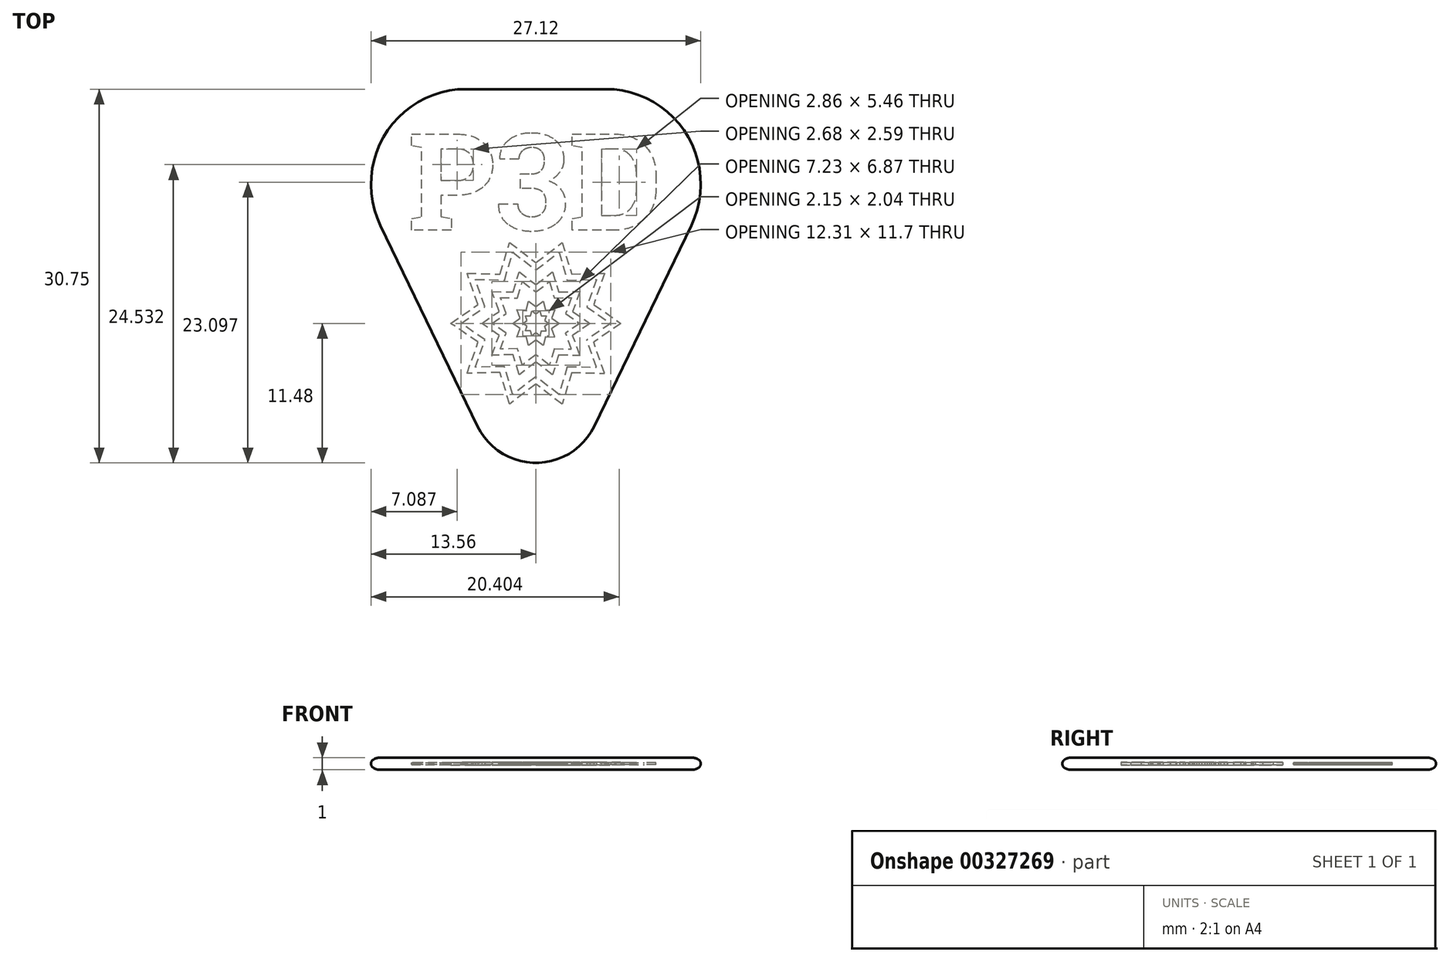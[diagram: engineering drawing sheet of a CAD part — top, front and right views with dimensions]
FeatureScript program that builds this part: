
annotation { "Feature Type Name" : "Feature", "Feature Type Description" : "" }
export const myFeature = defineFeature(function(context is Context, id is Id, definition is map)
    precondition{}
    {
        {
            var Q0;
            Q0=qCreatedBy(makeId("Top.planeOp"),FACE);
            var sketch = newSketch(context, id + "F0", { "sketchPlane" : qUnion([Q0])});
            skLineSegment(sketch, "E0", {"start": v(-5.74, 12.45) * mm, "end": v(5.74, 12.45) * mm});
            skLineSegment(sketch, "E1", {"start": v(12.95, 0.97) * mm, "end": v(4.95, -15.56) * mm});
            skLineSegment(sketch, "E2", {"start": v(-4.95, -15.56) * mm, "end": v(-12.95, 0.97) * mm});
            skPoint(sketch, "E3.visualSharp", {"position": v(-18.5, 12.45) * mm});
            skArc(sketch, "E3.filletArc", {"start": v(-5.74, 12.45) * mm, "mid": v(-12.52, 8.7) * mm, "end": v(-12.95, 0.97) * mm});
            skPoint(sketch, "E4.visualSharp", {"position": v(18.5, 12.45) * mm});
            skArc(sketch, "E4.filletArc", {"start": v(12.95, 0.97) * mm, "mid": v(12.52, 8.7) * mm, "end": v(5.74, 12.45) * mm});
            skPoint(sketch, "E5.visualSharp", {"position": v(0, -25.8) * mm});
            skArc(sketch, "E5.filletArc", {"start": v(-4.95, -15.56) * mm, "mid": v(0, -18.66) * mm, "end": v(4.95, -15.56) * mm});
            skSolve(sketch);
        }
        {
            var Q0;
            Q0=makeQuery(id+"F0.imprint","IMPRINT",FACE,{"disambiguationData":[TD([[makeQuery(id+"F0.imprint","IMPRINT",EDGE,{"derivedFrom":sQuery(id+"F0.wireOp",EDGE,"E0")}),-1.0]])]});
            extrude(context, id + "F1", {"entities" : qUnion([Q0]), "endBound" : BoundingType.SYMMETRIC, "depth" : 1 * mm, "offsetDistance" : 25 * mm});
        }
        {
            var Q0;
            Q0=makeQuery(id+"F1.opExtrude","CAP_EDGE",EDGE,{"disambiguationData":[OSD([sQuery(id+"F0.wireOp",EDGE,"E1")])],"isStart":false});
            var Q1;
            Q1=makeQuery(id+"F1.opExtrude","CAP_EDGE",EDGE,{"disambiguationData":[OSD([sQuery(id+"F0.wireOp",EDGE,"E1")])],"isStart":true});
            chamfer(context, id + "F2", {"entities" : qUnion([Q0, Q1]), "chamferType" : ChamferType.OFFSET_ANGLE, "width" : 0.5 * mm, "oppositeDirection" : false, "angle" : 45 * degree, "tangentPropagation" : true});
        }
        {
            var Q0;
            {var subQ0=sQuery(id+"F0.wireOp",EDGE,"E2");Q0=makeQuery(id+"F2.opChamfer","BLEND_EDGE",EDGE,{"blendedFrom":[makeQuery(id+"F1.opExtrude","CAP_EDGE",EDGE,{"disambiguationData":[OSD([subQ0])],"isStart":false}),makeQuery(id+"F1.opExtrude","CAP_FACE",FACE,{"disambiguationData":[OSD([sQuery(id+"F0.wireOp",EDGE,"E0"),sQuery(id+"F0.wireOp",EDGE,"E1"),subQ0,sQuery(id+"F0.wireOp",EDGE,"E3.filletArc"),sQuery(id+"F0.wireOp",EDGE,"E4.filletArc"),sQuery(id+"F0.wireOp",EDGE,"E5.filletArc")])],"isStart":false})],"blendedInto":[makeQuery(id+"F1.opExtrude","CAP_FACE",FACE,{"disambiguationData":[OSD([sQuery(id+"F0.wireOp",EDGE,"E0"),sQuery(id+"F0.wireOp",EDGE,"E1"),subQ0,sQuery(id+"F0.wireOp",EDGE,"E3.filletArc"),sQuery(id+"F0.wireOp",EDGE,"E4.filletArc"),sQuery(id+"F0.wireOp",EDGE,"E5.filletArc")])],"isStart":false})]});}
            var Q1;
            {var subQ0=sQuery(id+"F0.wireOp",EDGE,"E1");Q1=makeQuery(id+"F2.opChamfer","BLEND_EDGE",EDGE,{"blendedFrom":[makeQuery(id+"F1.opExtrude","CAP_EDGE",EDGE,{"disambiguationData":[OSD([subQ0])],"isStart":true}),makeQuery(id+"F1.opExtrude","CAP_FACE",FACE,{"disambiguationData":[OSD([sQuery(id+"F0.wireOp",EDGE,"E0"),subQ0,sQuery(id+"F0.wireOp",EDGE,"E2"),sQuery(id+"F0.wireOp",EDGE,"E3.filletArc"),sQuery(id+"F0.wireOp",EDGE,"E4.filletArc"),sQuery(id+"F0.wireOp",EDGE,"E5.filletArc")])],"isStart":true})],"blendedInto":[makeQuery(id+"F1.opExtrude","CAP_FACE",FACE,{"disambiguationData":[OSD([sQuery(id+"F0.wireOp",EDGE,"E0"),subQ0,sQuery(id+"F0.wireOp",EDGE,"E2"),sQuery(id+"F0.wireOp",EDGE,"E3.filletArc"),sQuery(id+"F0.wireOp",EDGE,"E4.filletArc"),sQuery(id+"F0.wireOp",EDGE,"E5.filletArc")])],"isStart":true})]});}
            fillet(context, id + "F3", {"entities" : qUnion([Q0, Q1]), "radius" : 1 * mm, "tangentPropagation" : true, "allowEdgeOverflow" : false});
        }
        {
            var Q0;
            Q0=qCreatedBy(makeId("Top.planeOp"),FACE);
            var sketch = newSketch(context, id + "F4", { "sketchPlane" : qUnion([Q0])});
            skText(sketch, "E6", { "text": "P3D", "fontName": "RobotoSlab-Bold.ttf"});
            const initialGuessF4  = {"E6": [-0.01054, 0.00067, 1, 0, 0.008]};
            skSetInitialGuess(sketch, initialGuessF4);
            skSolve(sketch);
        }
        {
            var Q0;
            Q0=qSketchRegion(id+"F4",true);
            extrude(context, id + "F5", {"entities" : qUnion([Q0]), "operationType" : NewBodyOperationType.REMOVE, "endBound" : BoundingType.SYMMETRIC, "oppositeDirection" : true, "depth" : 0.18 * mm, "offsetDistance" : 25 * mm});
        }
        {
            var Q0;
            {var subQ0=sQuery(id+"F0.wireOp",EDGE,"E2");Q0=makeQuery(id+"F2.opChamfer","BLEND_EDGE",EDGE,{"blendedFrom":[makeQuery(id+"F1.opExtrude","CAP_EDGE",EDGE,{"disambiguationData":[OSD([subQ0])],"isStart":true}),makeQuery(id+"F1.opExtrude","CAP_EDGE",EDGE,{"disambiguationData":[OSD([subQ0])],"isStart":false})],"blendedInto":[]});}
            fillet(context, id + "F6", {"entities" : qUnion([Q0]), "radius" : 0.4 * mm, "tangentPropagation" : true, "allowEdgeOverflow" : false});
        }
        {
            var Q0;
            Q0=qCreatedBy(makeId("Top.planeOp"),FACE);
            var sketch = newSketch(context, id + "F7", { "sketchPlane" : qUnion([Q0])});
            skCircle(sketch, "E7.cCircle", {"center": v(0, -7) * mm, "radius": 5 * mm, "construction": true});
            skLineSegment(sketch, "E8", {"start": v(-4.76, -5.45) * mm, "end": v(-5.66, -2.89) * mm});
            skLineSegment(sketch, "E9", {"start": v(-5.66, -2.89) * mm, "end": v(-2.94, -2.95) * mm});
            skLineSegment(sketch, "E10", {"start": v(-2.94, -2.95) * mm, "end": v(-2.16, -0.34) * mm});
            skLineSegment(sketch, "E11", {"start": v(-2.16, -0.34) * mm, "end": v(0, -2) * mm});
            skLineSegment(sketch, "E12", {"start": v(0, -2) * mm, "end": v(2.16, -0.34) * mm});
            skLineSegment(sketch, "E13", {"start": v(2.16, -0.34) * mm, "end": v(2.94, -2.95) * mm});
            skLineSegment(sketch, "E14", {"start": v(2.94, -2.95) * mm, "end": v(5.66, -2.89) * mm});
            skLineSegment(sketch, "E15", {"start": v(5.66, -2.89) * mm, "end": v(4.76, -5.45) * mm});
            skLineSegment(sketch, "E16", {"start": v(4.76, -5.45) * mm, "end": v(7, -7) * mm});
            skLineSegment(sketch, "E17", {"start": v(7, -7) * mm, "end": v(4.76, -8.55) * mm});
            skLineSegment(sketch, "E18", {"start": v(2.94, -11.05) * mm, "end": v(5.66, -11.11) * mm});
            skLineSegment(sketch, "E19", {"start": v(5.66, -11.11) * mm, "end": v(4.76, -8.55) * mm});
            skLineSegment(sketch, "E20", {"start": v(2.94, -11.05) * mm, "end": v(2.16, -13.66) * mm});
            skLineSegment(sketch, "E21", {"start": v(2.16, -13.66) * mm, "end": v(0, -12) * mm});
            skLineSegment(sketch, "E22", {"start": v(0, -12) * mm, "end": v(-2.16, -13.66) * mm});
            skLineSegment(sketch, "E23", {"start": v(-2.16, -13.66) * mm, "end": v(-2.94, -11.05) * mm});
            skLineSegment(sketch, "E24", {"start": v(-2.94, -11.05) * mm, "end": v(-5.66, -11.11) * mm});
            skLineSegment(sketch, "E25", {"start": v(-5.66, -11.11) * mm, "end": v(-4.76, -8.55) * mm});
            skLineSegment(sketch, "E26", {"start": v(-4.76, -8.55) * mm, "end": v(-7, -7) * mm});
            skLineSegment(sketch, "E27", {"start": v(-7, -7) * mm, "end": v(-4.76, -5.45) * mm});
            skCircle(sketch, "E28", {"center": v(0, -7) * mm, "radius": 7 * mm, "construction": true});
            skLineSegment(sketch, "E29.0", {"start": v(4.18, -5.64) * mm, "end": v(6.15, -7) * mm});
            skLineSegment(sketch, "E29.1", {"start": v(4.98, -3.38) * mm, "end": v(4.18, -5.64) * mm});
            skLineSegment(sketch, "E29.2", {"start": v(2.58, -3.44) * mm, "end": v(4.98, -3.38) * mm});
            skLineSegment(sketch, "E29.3", {"start": v(1.9, -1.15) * mm, "end": v(2.58, -3.44) * mm});
            skLineSegment(sketch, "E29.4", {"start": v(0, -2.6) * mm, "end": v(1.9, -1.15) * mm});
            skLineSegment(sketch, "E29.5", {"start": v(6.15, -7) * mm, "end": v(4.18, -8.36) * mm});
            skLineSegment(sketch, "E29.6", {"start": v(-1.9, -1.15) * mm, "end": v(0, -2.6) * mm});
            skLineSegment(sketch, "E29.7", {"start": v(-2.58, -3.44) * mm, "end": v(-1.9, -1.15) * mm});
            skLineSegment(sketch, "E29.8", {"start": v(-4.98, -3.38) * mm, "end": v(-2.58, -3.44) * mm});
            skLineSegment(sketch, "E29.9", {"start": v(-4.18, -5.64) * mm, "end": v(-4.98, -3.38) * mm});
            skLineSegment(sketch, "E29.10", {"start": v(1.9, -12.85) * mm, "end": v(0, -11.4) * mm});
            skLineSegment(sketch, "E29.11", {"start": v(2.58, -10.56) * mm, "end": v(1.9, -12.85) * mm});
            skLineSegment(sketch, "E29.12", {"start": v(2.58, -10.56) * mm, "end": v(4.98, -10.62) * mm});
            skLineSegment(sketch, "E29.13", {"start": v(4.98, -10.62) * mm, "end": v(4.18, -8.36) * mm});
            skLineSegment(sketch, "E29.14", {"start": v(0, -11.4) * mm, "end": v(-1.9, -12.85) * mm});
            skLineSegment(sketch, "E29.15", {"start": v(-1.9, -12.85) * mm, "end": v(-2.58, -10.56) * mm});
            skLineSegment(sketch, "E29.16", {"start": v(-2.58, -10.56) * mm, "end": v(-4.98, -10.62) * mm});
            skLineSegment(sketch, "E29.17", {"start": v(-4.98, -10.62) * mm, "end": v(-4.18, -8.36) * mm});
            skLineSegment(sketch, "E29.18", {"start": v(-4.18, -8.36) * mm, "end": v(-6.15, -7) * mm});
            skLineSegment(sketch, "E29.19", {"start": v(-6.15, -7) * mm, "end": v(-4.18, -5.64) * mm});
            skLineSegment(sketch, "E30.0", {"start": v(-4.46, -7) * mm, "end": v(-3.03, -6.02) * mm});
            skLineSegment(sketch, "E30.1", {"start": v(-3.03, -7.98) * mm, "end": v(-4.46, -7) * mm});
            skLineSegment(sketch, "E30.2", {"start": v(-3.6, -9.62) * mm, "end": v(-3.03, -7.98) * mm});
            skLineSegment(sketch, "E30.3", {"start": v(-1.87, -9.58) * mm, "end": v(-3.6, -9.62) * mm});
            skLineSegment(sketch, "E30.4", {"start": v(-1.38, -11.24) * mm, "end": v(-1.87, -9.58) * mm});
            skLineSegment(sketch, "E30.5", {"start": v(-3.03, -6.02) * mm, "end": v(-3.6, -4.38) * mm});
            skLineSegment(sketch, "E30.6", {"start": v(0, -10.19) * mm, "end": v(-1.38, -11.24) * mm});
            skLineSegment(sketch, "E30.7", {"start": v(1.38, -11.24) * mm, "end": v(0, -10.19) * mm});
            skLineSegment(sketch, "E30.8", {"start": v(1.87, -9.58) * mm, "end": v(1.38, -11.24) * mm});
            skLineSegment(sketch, "E30.9", {"start": v(1.87, -9.58) * mm, "end": v(3.6, -9.62) * mm});
            skLineSegment(sketch, "E30.10", {"start": v(0, -3.81) * mm, "end": v(1.38, -2.76) * mm});
            skLineSegment(sketch, "E30.11", {"start": v(-1.38, -2.76) * mm, "end": v(0, -3.81) * mm});
            skLineSegment(sketch, "E30.12", {"start": v(-1.87, -4.42) * mm, "end": v(-1.38, -2.76) * mm});
            skLineSegment(sketch, "E30.13", {"start": v(-3.6, -4.38) * mm, "end": v(-1.87, -4.42) * mm});
            skLineSegment(sketch, "E30.14", {"start": v(1.38, -2.76) * mm, "end": v(1.87, -4.42) * mm});
            skLineSegment(sketch, "E30.15", {"start": v(1.87, -4.42) * mm, "end": v(3.6, -4.38) * mm});
            skLineSegment(sketch, "E30.16", {"start": v(3.6, -4.38) * mm, "end": v(3.03, -6.02) * mm});
            skLineSegment(sketch, "E30.17", {"start": v(3.03, -6.02) * mm, "end": v(4.46, -7) * mm});
            skLineSegment(sketch, "E30.18", {"start": v(4.46, -7) * mm, "end": v(3.03, -7.98) * mm});
            skLineSegment(sketch, "E30.19", {"start": v(3.6, -9.62) * mm, "end": v(3.03, -7.98) * mm});
            skLineSegment(sketch, "E31.0", {"start": v(-2.45, -6.2) * mm, "end": v(-2.92, -4.88) * mm});
            skLineSegment(sketch, "E31.1", {"start": v(-3.61, -7) * mm, "end": v(-2.45, -6.2) * mm});
            skLineSegment(sketch, "E31.2", {"start": v(-2.45, -7.8) * mm, "end": v(-3.61, -7) * mm});
            skLineSegment(sketch, "E31.3", {"start": v(-2.92, -9.12) * mm, "end": v(-2.45, -7.8) * mm});
            skLineSegment(sketch, "E31.4", {"start": v(-1.52, -9.09) * mm, "end": v(-2.92, -9.12) * mm});
            skLineSegment(sketch, "E31.5", {"start": v(-2.92, -4.88) * mm, "end": v(-1.52, -4.91) * mm});
            skLineSegment(sketch, "E31.6", {"start": v(-1.12, -10.44) * mm, "end": v(-1.52, -9.09) * mm});
            skLineSegment(sketch, "E31.7", {"start": v(0, -9.58) * mm, "end": v(-1.12, -10.44) * mm});
            skLineSegment(sketch, "E31.8", {"start": v(1.12, -10.44) * mm, "end": v(0, -9.58) * mm});
            skLineSegment(sketch, "E31.9", {"start": v(1.52, -9.09) * mm, "end": v(1.12, -10.44) * mm});
            skLineSegment(sketch, "E31.10", {"start": v(1.12, -3.56) * mm, "end": v(1.52, -4.91) * mm});
            skLineSegment(sketch, "E31.11", {"start": v(0, -4.42) * mm, "end": v(1.12, -3.56) * mm});
            skLineSegment(sketch, "E31.12", {"start": v(-1.12, -3.56) * mm, "end": v(0, -4.42) * mm});
            skLineSegment(sketch, "E31.13", {"start": v(-1.52, -4.91) * mm, "end": v(-1.12, -3.56) * mm});
            skLineSegment(sketch, "E31.14", {"start": v(1.52, -4.91) * mm, "end": v(2.92, -4.88) * mm});
            skLineSegment(sketch, "E31.15", {"start": v(2.92, -4.88) * mm, "end": v(2.45, -6.2) * mm});
            skLineSegment(sketch, "E31.16", {"start": v(2.45, -6.2) * mm, "end": v(3.61, -7) * mm});
            skLineSegment(sketch, "E31.17", {"start": v(3.61, -7) * mm, "end": v(2.45, -7.8) * mm});
            skLineSegment(sketch, "E31.18", {"start": v(2.92, -9.12) * mm, "end": v(2.45, -7.8) * mm});
            skLineSegment(sketch, "E31.19", {"start": v(1.52, -9.09) * mm, "end": v(2.92, -9.12) * mm});
            skLineSegment(sketch, "E32.0", {"start": v(-1.92, -7) * mm, "end": v(-1.3, -6.58) * mm});
            skLineSegment(sketch, "E32.1", {"start": v(-1.3, -7.42) * mm, "end": v(-1.92, -7) * mm});
            skLineSegment(sketch, "E32.2", {"start": v(-1.55, -8.13) * mm, "end": v(-1.3, -7.42) * mm});
            skLineSegment(sketch, "E32.3", {"start": v(-0.8, -8.1) * mm, "end": v(-1.55, -8.13) * mm});
            skLineSegment(sketch, "E32.4", {"start": v(-0.6, -8.83) * mm, "end": v(-0.8, -8.1) * mm});
            skLineSegment(sketch, "E32.5", {"start": v(-1.3, -6.58) * mm, "end": v(-1.55, -5.87) * mm});
            skLineSegment(sketch, "E32.6", {"start": v(0, -8.37) * mm, "end": v(-0.6, -8.83) * mm});
            skLineSegment(sketch, "E32.7", {"start": v(0.6, -8.83) * mm, "end": v(0, -8.37) * mm});
            skLineSegment(sketch, "E32.8", {"start": v(0.8, -8.1) * mm, "end": v(0.6, -8.83) * mm});
            skLineSegment(sketch, "E32.9", {"start": v(0.8, -8.1) * mm, "end": v(1.55, -8.13) * mm});
            skLineSegment(sketch, "E32.10", {"start": v(0, -5.63) * mm, "end": v(0.6, -5.17) * mm});
            skLineSegment(sketch, "E32.11", {"start": v(-0.6, -5.17) * mm, "end": v(0, -5.63) * mm});
            skLineSegment(sketch, "E32.12", {"start": v(-0.8, -5.9) * mm, "end": v(-0.6, -5.17) * mm});
            skLineSegment(sketch, "E32.13", {"start": v(-1.55, -5.87) * mm, "end": v(-0.8, -5.9) * mm});
            skLineSegment(sketch, "E32.14", {"start": v(0.6, -5.17) * mm, "end": v(0.8, -5.9) * mm});
            skLineSegment(sketch, "E32.15", {"start": v(0.8, -5.9) * mm, "end": v(1.55, -5.87) * mm});
            skLineSegment(sketch, "E32.16", {"start": v(1.55, -5.87) * mm, "end": v(1.3, -6.58) * mm});
            skLineSegment(sketch, "E32.17", {"start": v(1.3, -6.58) * mm, "end": v(1.92, -7) * mm});
            skLineSegment(sketch, "E32.18", {"start": v(1.92, -7) * mm, "end": v(1.3, -7.42) * mm});
            skLineSegment(sketch, "E32.19", {"start": v(1.55, -8.13) * mm, "end": v(1.3, -7.42) * mm});
            skLineSegment(sketch, "E33.0", {"start": v(-0.45, -6.38) * mm, "end": v(-0.33, -5.98) * mm});
            skLineSegment(sketch, "E33.1", {"start": v(-0.87, -6.37) * mm, "end": v(-0.45, -6.38) * mm});
            skLineSegment(sketch, "E33.2", {"start": v(-0.73, -6.76) * mm, "end": v(-0.87, -6.37) * mm});
            skLineSegment(sketch, "E33.3", {"start": v(-1.07, -7) * mm, "end": v(-0.73, -6.76) * mm});
            skLineSegment(sketch, "E33.4", {"start": v(-0.73, -7.24) * mm, "end": v(-1.07, -7) * mm});
            skLineSegment(sketch, "E33.5", {"start": v(-0.33, -5.98) * mm, "end": v(0, -6.23) * mm});
            skLineSegment(sketch, "E33.6", {"start": v(-0.87, -7.63) * mm, "end": v(-0.73, -7.24) * mm});
            skLineSegment(sketch, "E33.7", {"start": v(-0.45, -7.62) * mm, "end": v(-0.87, -7.63) * mm});
            skLineSegment(sketch, "E33.8", {"start": v(-0.33, -8.02) * mm, "end": v(-0.45, -7.62) * mm});
            skLineSegment(sketch, "E33.9", {"start": v(0, -7.77) * mm, "end": v(-0.33, -8.02) * mm});
            skLineSegment(sketch, "E33.10", {"start": v(0.87, -6.37) * mm, "end": v(0.73, -6.76) * mm});
            skLineSegment(sketch, "E33.11", {"start": v(0.45, -6.38) * mm, "end": v(0.87, -6.37) * mm});
            skLineSegment(sketch, "E33.12", {"start": v(0.33, -5.98) * mm, "end": v(0.45, -6.38) * mm});
            skLineSegment(sketch, "E33.13", {"start": v(0, -6.23) * mm, "end": v(0.33, -5.98) * mm});
            skLineSegment(sketch, "E33.14", {"start": v(0.73, -6.76) * mm, "end": v(1.07, -7) * mm});
            skLineSegment(sketch, "E33.15", {"start": v(1.07, -7) * mm, "end": v(0.73, -7.24) * mm});
            skLineSegment(sketch, "E33.16", {"start": v(0.87, -7.63) * mm, "end": v(0.73, -7.24) * mm});
            skLineSegment(sketch, "E33.17", {"start": v(0.45, -7.62) * mm, "end": v(0.87, -7.63) * mm});
            skLineSegment(sketch, "E33.18", {"start": v(0.45, -7.62) * mm, "end": v(0.33, -8.02) * mm});
            skLineSegment(sketch, "E33.19", {"start": v(0.33, -8.02) * mm, "end": v(0, -7.77) * mm});
            skSolve(sketch);
        }
        {
            var Q0;
            Q0=makeQuery(id+"F7.imprint","IMPRINT",FACE,{"disambiguationData":[TD([[makeQuery(id+"F7.imprint","IMPRINT",EDGE,{"derivedFrom":sQuery(id+"F7.wireOp",EDGE,"E8")}),-1.0]])]});
            var Q1;
            Q1=makeQuery(id+"F7.imprint","IMPRINT",FACE,{"disambiguationData":[TD([[makeQuery(id+"F7.imprint","IMPRINT",EDGE,{"derivedFrom":sQuery(id+"F7.wireOp",EDGE,"E30.0")}),-1.0]])]});
            var Q2;
            Q2=makeQuery(id+"F7.imprint","IMPRINT",FACE,{"disambiguationData":[TD([[makeQuery(id+"F7.imprint","IMPRINT",EDGE,{"derivedFrom":sQuery(id+"F7.wireOp",EDGE,"E32.0")}),-1.0]])]});
            extrude(context, id + "F8", {"entities" : qUnion([Q0, Q1, Q2]), "operationType" : NewBodyOperationType.REMOVE, "endBound" : BoundingType.SYMMETRIC, "depth" : 0.2 * mm, "offsetDistance" : 25 * mm});
        }
    });
